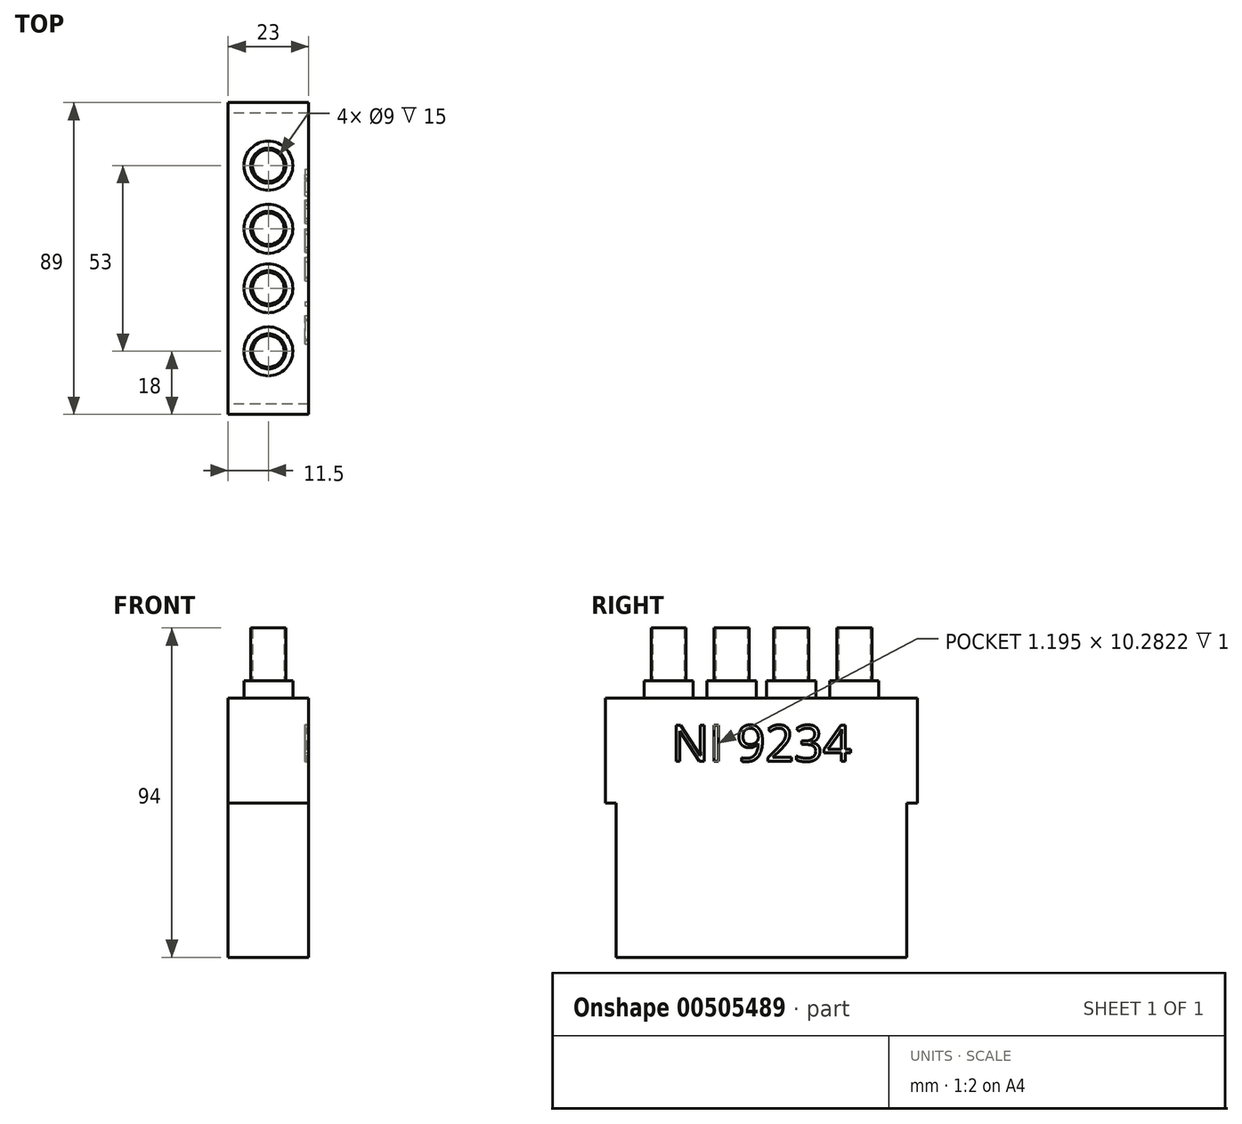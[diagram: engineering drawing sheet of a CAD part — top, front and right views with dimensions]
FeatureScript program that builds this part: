
annotation { "Feature Type Name" : "Feature", "Feature Type Description" : "" }
export const myFeature = defineFeature(function(context is Context, id is Id, definition is map)
    precondition{}
    {
        {
            var Q0;
            Q0=qCreatedBy(makeId("Right.planeOp"),FACE);
            var sketch = newSketch(context, id + "F0", { "sketchPlane" : qUnion([Q0])});
            skLineSegment(sketch, "E0.bottom", {"start": v(0, 0) * mm, "end": v(83, 0) * mm});
            skLineSegment(sketch, "E0.left", {"start": v(0, 0) * mm, "end": v(0, 44) * mm});
            skLineSegment(sketch, "E0.right", {"start": v(83, 0) * mm, "end": v(83, 44) * mm});
            skLineSegment(sketch, "E1.0", {"start": v(-3, 74) * mm, "end": v(86, 74) * mm});
            skLineSegment(sketch, "E2.0", {"start": v(-3, 44) * mm, "end": v(-3, 74) * mm});
            skLineSegment(sketch, "E3", {"start": v(0, 44) * mm, "end": v(-3, 44) * mm});
            skLineSegment(sketch, "E4", {"start": v(83, 44) * mm, "end": v(86, 44) * mm});
            skLineSegment(sketch, "E5", {"start": v(86, 44) * mm, "end": v(86, 74) * mm});
            skSolve(sketch);
        }
        {
            var Q0;
            Q0 = qSketchRegion(id + "F0", true);
            extrude(context, id + "F1", {"entities" : qUnion([Q0]), "depth" : 23 * mm});
        }
        {
            var Q0;
            Q0=makeQuery(id+"F1.opExtrude","SWEPT_FACE",FACE,{"disambiguationData":[OSD([sQuery(id+"F0.wireOp",EDGE,"E1.0")])]});
            var sketch = newSketch(context, id + "F2", { "sketchPlane" : qUnion([Q0])});
            skCircle(sketch, "E6", {"center": v(11.5, 15) * mm, "radius": 5 * mm});
            skCircle(sketch, "E7", {"center": v(11.5, 68) * mm, "radius": 5 * mm});
            skCircle(sketch, "E8", {"center": v(11.5, 50) * mm, "radius": 5 * mm});
            skCircle(sketch, "E9", {"center": v(11.5, 33) * mm, "radius": 5 * mm});
            skCircle(sketch, "E10", {"center": v(11.5, 68) * mm, "radius": 4.5 * mm});
            skCircle(sketch, "E11", {"center": v(11.5, 50) * mm, "radius": 4.5 * mm});
            skCircle(sketch, "E12", {"center": v(11.5, 33) * mm, "radius": 4.5 * mm});
            skCircle(sketch, "E13", {"center": v(11.5, 15) * mm, "radius": 4.5 * mm});
            skSolve(sketch);
        }
        {
            var Q0;
            Q0 = qSketchRegion(id + "F2", true);
            extrude(context, id + "F3", {"entities" : qUnion([Q0]), "operationType" : NewBodyOperationType.ADD, "depth" : 20 * mm});
        }
        {
            var Q0;
            {var subQ3=sQuery(id+"F0.wireOp",EDGE,"E2.0");var subQ4=sQuery(id+"F0.wireOp",EDGE,"E1.0");Q0=makeQuery(id+"F3.boolean.opBoolean","SPLIT",FACE,{"disambiguationData":[TD([makeQuery(id+"F1.opExtrude","SWEPT_FACE",FACE,{"disambiguationData":[OSD([subQ3])]})])],"derivedFrom":makeQuery(id+"F1.opExtrude","SWEPT_FACE",FACE,{"disambiguationData":[OSD([subQ4])]})});}
            var sketch = newSketch(context, id + "F4", { "sketchPlane" : qUnion([Q0])});
            skCircle(sketch, "E14", {"center": v(11.5, 68) * mm, "radius": 7 * mm});
            skCircle(sketch, "E15", {"center": v(11.5, 50) * mm, "radius": 7 * mm});
            skCircle(sketch, "E16", {"center": v(11.5, 33) * mm, "radius": 7 * mm});
            skCircle(sketch, "E17", {"center": v(11.5, 15) * mm, "radius": 7 * mm});
            skSolve(sketch);
        }
        {
            var Q0;
            Q0 = qSketchRegion(id + "F4", true);
            extrude(context, id + "F5", {"entities" : qUnion([Q0]), "operationType" : NewBodyOperationType.ADD, "depth" : 5 * mm});
        }
        {
            var Q0;
            Q0=makeQuery(id+"F1.opExtrude","CAP_FACE",FACE,{"disambiguationData":[OSD([sQuery(id+"F0.wireOp",EDGE,"E0.bottom"),sQuery(id+"F0.wireOp",EDGE,"E0.left"),sQuery(id+"F0.wireOp",EDGE,"E0.right"),sQuery(id+"F0.wireOp",EDGE,"E1.0"),sQuery(id+"F0.wireOp",EDGE,"E2.0"),sQuery(id+"F0.wireOp",EDGE,"E3"),sQuery(id+"F0.wireOp",EDGE,"E4"),sQuery(id+"F0.wireOp",EDGE,"E5")])],"isStart":false});
            var sketch = newSketch(context, id + "F6", { "sketchPlane" : qUnion([Q0])});
            skText(sketch, "E18", { "text": "NI 9234", "fontName": "OpenSans-Regular.ttf"});
            const initialGuessF6  = {"E18": [0.01572, 0.05596, 1, 0, 0.01037]};
            skSetInitialGuess(sketch, initialGuessF6);
            skSolve(sketch);
        }
        {
            var Q0;
            Q0 = qSketchRegion(id + "F6", true);
            extrude(context, id + "F7", {"entities" : qUnion([Q0]), "operationType" : NewBodyOperationType.REMOVE, "oppositeDirection" : true, "depth" : 1 * mm});
        }
    });
